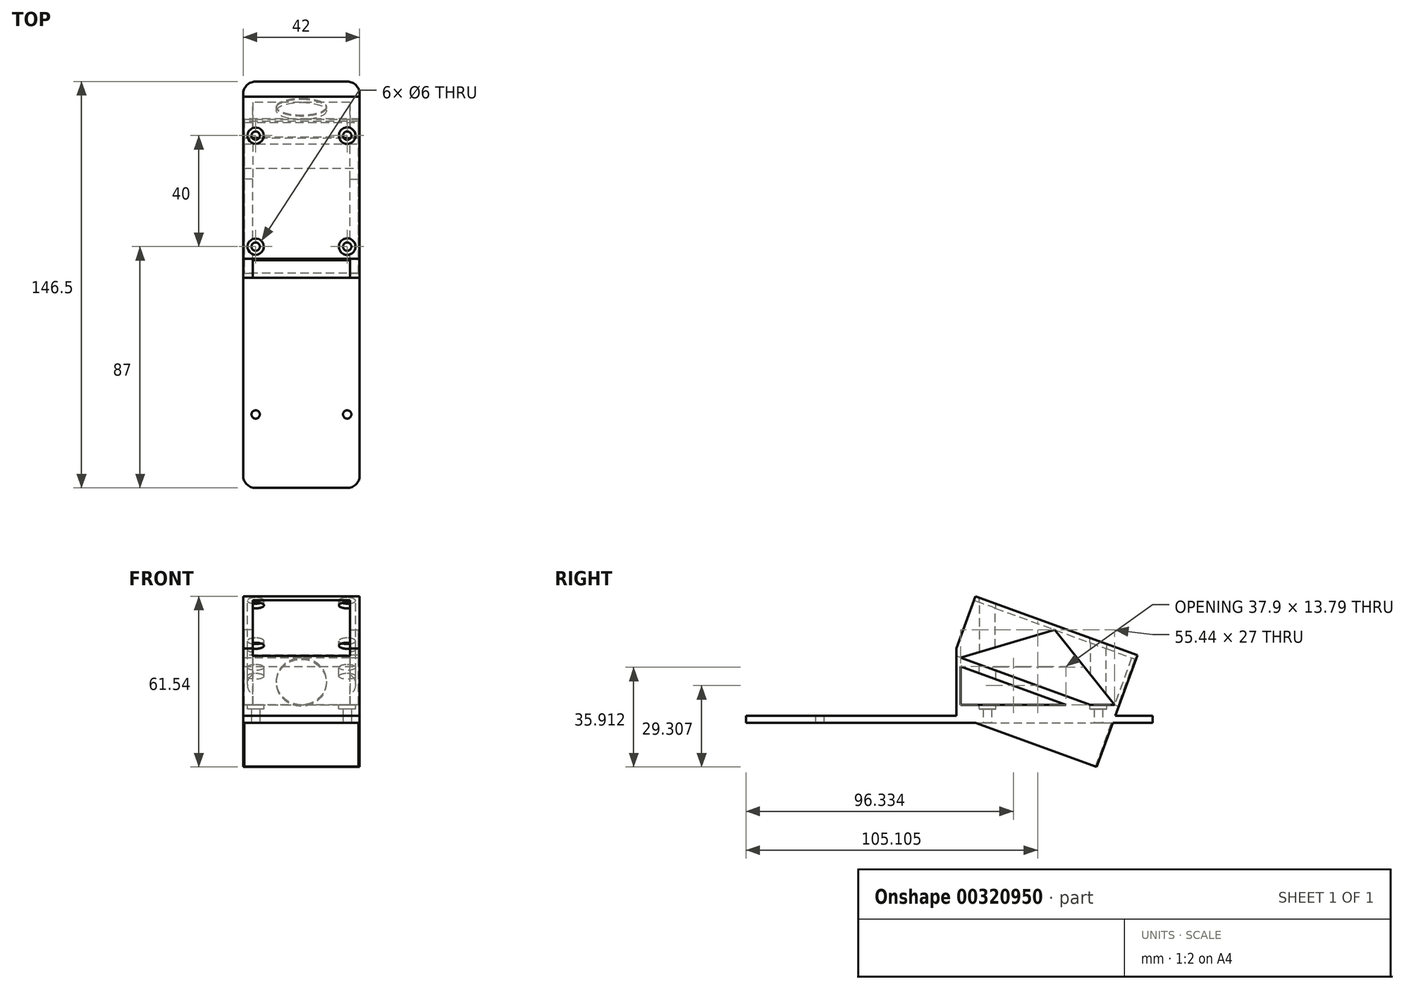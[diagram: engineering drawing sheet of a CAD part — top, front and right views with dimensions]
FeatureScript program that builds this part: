
annotation { "Feature Type Name" : "Feature", "Feature Type Description" : "" }
export const myFeature = defineFeature(function(context is Context, id is Id, definition is map)
    precondition{}
    {
        {
            var Q0;
            Q0=qCreatedBy(makeId("Top.planeOp"),FACE);
            var sketch = newSketch(context, id + "F0", { "sketchPlane" : qUnion([Q0])});
            skLineSegment(sketch, "E0.left", {"start": v(-21, 71.75) * mm, "end": v(-21, -44.25) * mm});
            skLineSegment(sketch, "E0.right", {"start": v(21, 72.25) * mm, "end": v(21, -44.25) * mm});
            skCircle(sketch, "E1", {"center": v(16.5, 72.25) * mm, "radius": 1.5 * mm});
            skCircle(sketch, "E2", {"center": v(-16.5, 72.25) * mm, "radius": 1.5 * mm});
            skCircle(sketch, "E3", {"center": v(16.5, 32.25) * mm, "radius": 1.5 * mm});
            skCircle(sketch, "E4", {"center": v(-16.5, 32.25) * mm, "radius": 1.5 * mm});
            skCircle(sketch, "E5", {"center": v(16.5, -28.25) * mm, "radius": 1.5 * mm});
            skCircle(sketch, "E6", {"center": v(-16.5, -28.25) * mm, "radius": 1.5 * mm});
            skPoint(sketch, "E7", {"position": v(-21, -54.75) * mm});
            skLineSegment(sketch, "E8", {"start": v(-21, -44.25) * mm, "end": v(-21, -50.25) * mm});
            skLineSegment(sketch, "E9", {"start": v(21, -44.25) * mm, "end": v(21, -50.25) * mm});
            skLineSegment(sketch, "E10", {"start": v(16.5, -54.75) * mm, "end": v(-16.5, -54.75) * mm});
            skArc(sketch, "E11.filletArc", {"start": v(-21, -50.25) * mm, "mid": v(-19.68, -53.43) * mm, "end": v(-16.5, -54.75) * mm});
            skPoint(sketch, "E12.visualSharp", {"position": v(21, -54.75) * mm});
            skArc(sketch, "E12.filletArc", {"start": v(16.5, -54.75) * mm, "mid": v(19.68, -53.43) * mm, "end": v(21, -50.25) * mm});
            skLineSegment(sketch, "E13", {"start": v(-21, 71.75) * mm, "end": v(-21, 87.25) * mm});
            skLineSegment(sketch, "E14", {"start": v(-16.5, 91.75) * mm, "end": v(16.5, 91.75) * mm});
            skLineSegment(sketch, "E15", {"start": v(21, 87.25) * mm, "end": v(21, 72.25) * mm});
            skPoint(sketch, "E16.visualSharp", {"position": v(-21, 91.75) * mm});
            skArc(sketch, "E16.filletArc", {"start": v(-16.5, 91.75) * mm, "mid": v(-19.68, 90.43) * mm, "end": v(-21, 87.25) * mm});
            skPoint(sketch, "E17.visualSharp", {"position": v(21, 91.75) * mm});
            skArc(sketch, "E17.filletArc", {"start": v(21, 87.25) * mm, "mid": v(19.68, 90.43) * mm, "end": v(16.5, 91.75) * mm});
            skSolve(sketch);
        }
        {
            var Q0;
            Q0=qSketchRegion(id+"F0",true);
            extrude(context, id + "F1", {"entities" : qUnion([Q0]), "depth" : 2.5 * mm});
        }
        {
            var Q0;
            Q0=qCreatedBy(makeId("Right.planeOp"),FACE);
            var sketch = newSketch(context, id + "F2", { "sketchPlane" : qUnion([Q0])});
            skLineSegment(sketch, "E18.1.1", {"start": v(91.75, 20.68) * mm, "end": v(85.6, 3.76) * mm, "construction": true});
            skLineSegment(sketch, "E18.1.2", {"start": v(22.63, 26.68) * mm, "end": v(28.8, 43.6) * mm});
            skLineSegment(sketch, "E19", {"start": v(84.23, 23.41) * mm, "end": v(78.08, 6.5) * mm});
            skLineSegment(sketch, "E20", {"start": v(28.8, 43.6) * mm, "end": v(84.23, 23.41) * mm});
            skLineSegment(sketch, "E21", {"start": v(91.75, 20.68) * mm, "end": v(85.74, 22.87) * mm, "construction": true});
            skLineSegment(sketch, "E22", {"start": v(85.6, 3.76) * mm, "end": v(79.58, 5.95) * mm, "construction": true});
            skLineSegment(sketch, "E23", {"start": v(22.63, 6.5) * mm, "end": v(22.63, 26.68) * mm});
            skLineSegment(sketch, "E24", {"start": v(79.58, 5.95) * mm, "end": v(78.32, 2.5) * mm});
            skLineSegment(sketch, "E25", {"start": v(78.32, 2.5) * mm, "end": v(22.63, 2.5) * mm});
            skLineSegment(sketch, "E26", {"start": v(86.28, 24.37) * mm, "end": v(26.52, 46.12) * mm});
            skLineSegment(sketch, "E27", {"start": v(79.58, 5.95) * mm, "end": v(86.28, 24.37) * mm});
            skLineSegment(sketch, "E28", {"start": v(27.87, 45.63) * mm, "end": v(21.03, 26.84) * mm});
            skLineSegment(sketch, "E29", {"start": v(22.63, 2.5) * mm, "end": v(21.03, 2.5) * mm});
            skLineSegment(sketch, "E30", {"start": v(21.03, 2.5) * mm, "end": v(21.03, 26.84) * mm});
            skLineSegment(sketch, "E31", {"start": v(78.08, 6.5) * mm, "end": v(22.63, 6.5) * mm});
            skSolve(sketch);
        }
        {
            var Q0;
            Q0=qSketchRegion(id+"F2",true);
            extrude(context, id + "F3", {"entities" : qUnion([Q0]), "depth" : 21 * mm, "hasSecondDirection" : true, "secondDirectionOppositeDirection" : true, "secondDirectionDepth" : 21 * mm});
        }
        {
            var Q0;
            Q0=makeQuery(id+"F3.opExtrude","CAP_FACE",FACE,{"disambiguationData":[OSD([sQuery(id+"F2.wireOp",EDGE,"E18.1.2"),sQuery(id+"F2.wireOp",EDGE,"E19"),sQuery(id+"F2.wireOp",EDGE,"E20"),sQuery(id+"F2.wireOp",EDGE,"E23"),sQuery(id+"F2.wireOp",EDGE,"E24"),sQuery(id+"F2.wireOp",EDGE,"E25"),sQuery(id+"F2.wireOp",EDGE,"E26"),sQuery(id+"F2.wireOp",EDGE,"E27"),sQuery(id+"F2.wireOp",EDGE,"E28"),sQuery(id+"F2.wireOp",EDGE,"E29"),sQuery(id+"F2.wireOp",EDGE,"E30"),sQuery(id+"F2.wireOp",EDGE,"E31")])],"isStart":false});
            var sketch = newSketch(context, id + "F4", { "sketchPlane" : qUnion([Q0])});
            skLineSegment(sketch, "E32", {"start": v(78.08, 6.5) * mm, "end": v(22.63, 26.68) * mm, "construction": true});
            skLineSegment(sketch, "E33", {"start": v(69.3, 6.5) * mm, "end": v(22.63, 23.49) * mm});
            skLineSegment(sketch, "E34", {"start": v(60.53, 6.5) * mm, "end": v(22.63, 20.3) * mm});
            skLineSegment(sketch, "E35", {"start": v(69.3, 6.5) * mm, "end": v(60.53, 6.5) * mm});
            skLineSegment(sketch, "E36", {"start": v(22.63, 20.3) * mm, "end": v(22.63, 23.49) * mm});
            skPoint(sketch, "E37", {"position": v(56.51, 33.5) * mm});
            skLineSegment(sketch, "E38", {"start": v(84.23, 23.41) * mm, "end": v(78.08, 6.5) * mm});
            skLineSegment(sketch, "E39", {"start": v(84.23, 23.41) * mm, "end": v(56.51, 33.5) * mm});
            skLineSegment(sketch, "E40", {"start": v(28.8, 43.6) * mm, "end": v(22.63, 26.68) * mm});
            skLineSegment(sketch, "E41", {"start": v(56.51, 33.5) * mm, "end": v(28.8, 43.6) * mm});
            skLineSegment(sketch, "E42", {"start": v(22.63, 23.49) * mm, "end": v(56.51, 33.5) * mm});
            skLineSegment(sketch, "E43", {"start": v(22.63, 26.68) * mm, "end": v(22.63, 23.49) * mm});
            skLineSegment(sketch, "E44", {"start": v(78.08, 6.5) * mm, "end": v(56.51, 33.5) * mm});
            skSolve(sketch);
        }
        {
            var Q0;
            Q0=makeQuery(id+"F4.imprint","IMPRINT",FACE,{"disambiguationData":[TD([[makeQuery(id+"F4.imprint","IMPRINT",EDGE,{"derivedFrom":sQuery(id+"F4.wireOp",EDGE,"E33")}),1.0]])]});
            extrude(context, id + "F5", {"entities" : qUnion([Q0]), "operationType" : NewBodyOperationType.ADD, "oppositeDirection" : true, "depth" : 42 * mm});
        }
        {
            var Q0;
            Q0=makeQuery(id+"F4.imprint","IMPRINT",FACE,{"disambiguationData":[TD([[makeQuery(id+"F4.imprint","IMPRINT",EDGE,{"derivedFrom":sQuery(id+"F4.wireOp",EDGE,"E38")}),-1.0]])]});
            var Q1;
            Q1=makeQuery(id+"F4.imprint","IMPRINT",FACE,{"disambiguationData":[TD([[makeQuery(id+"F4.imprint","IMPRINT",EDGE,{"derivedFrom":sQuery(id+"F4.wireOp",EDGE,"E40")}),-1.0]])]});
            extrude(context, id + "F6", {"entities" : qUnion([Q0, Q1]), "operationType" : NewBodyOperationType.ADD, "oppositeDirection" : true, "depth" : 3.5 * mm});
        }
        {
            var Q0;
            Q0=makeQuery(id+"F5.boolean.opBoolean","MERGE",FACE,{"derivedFrom":[makeQuery(id+"F3.opExtrude","CAP_FACE",FACE,{"disambiguationData":[OSD([sQuery(id+"F2.wireOp",EDGE,"E18.1.2"),sQuery(id+"F2.wireOp",EDGE,"E19"),sQuery(id+"F2.wireOp",EDGE,"E20"),sQuery(id+"F2.wireOp",EDGE,"E23"),sQuery(id+"F2.wireOp",EDGE,"E24"),sQuery(id+"F2.wireOp",EDGE,"E25"),sQuery(id+"F2.wireOp",EDGE,"E26"),sQuery(id+"F2.wireOp",EDGE,"E27"),sQuery(id+"F2.wireOp",EDGE,"E28"),sQuery(id+"F2.wireOp",EDGE,"E29"),sQuery(id+"F2.wireOp",EDGE,"E30"),sQuery(id+"F2.wireOp",EDGE,"E31")])],"isStart":true}),makeQuery(id+"F5.opExtrude","CAP_FACE",FACE,{"disambiguationData":[OSD([sQuery(id+"F4.wireOp",EDGE,"E33"),sQuery(id+"F4.wireOp",EDGE,"E34"),sQuery(id+"F4.wireOp",EDGE,"E35"),sQuery(id+"F4.wireOp",EDGE,"E36")])],"isStart":false})]});
            var sketch = newSketch(context, id + "F7", { "sketchPlane" : qUnion([Q0])});
            skLineSegment(sketch, "E45.0", {"start": v(-22.63, 23.49) * mm, "end": v(-56.51, 33.5) * mm});
            skLineSegment(sketch, "E45.1", {"start": v(-22.63, 26.68) * mm, "end": v(-28.8, 43.6) * mm});
            skLineSegment(sketch, "E45.2", {"start": v(-22.63, 23.49) * mm, "end": v(-22.63, 26.68) * mm});
            skLineSegment(sketch, "E45.3", {"start": v(-28.8, 43.6) * mm, "end": v(-84.23, 23.41) * mm});
            skLineSegment(sketch, "E45.4", {"start": v(-84.23, 23.41) * mm, "end": v(-78.08, 6.5) * mm});
            skLineSegment(sketch, "E46", {"start": v(-78.08, 6.5) * mm, "end": v(-56.51, 33.5) * mm});
            skLineSegment(sketch, "E47.0", {"start": v(-60.53, 6.5) * mm, "end": v(-22.63, 6.5) * mm, "construction": true});
            skLineSegment(sketch, "E47.1", {"start": v(-87.25, 2.5) * mm, "end": v(50.25, 2.5) * mm, "construction": true});
            skSolve(sketch);
        }
        {
            var Q0;
            {var subQ0=sQuery(id+"F7.wireOp",EDGE,"E45.4");Q0=makeQuery(id+"F7.imprint","IMPRINT",FACE,{"disambiguationData":[TD([[makeQuery(id+"F7.imprint","IMPRINT",EDGE,{"derivedFrom":subQ0}),1.0]])]});}
            var Q1;
            {var subQ0=sQuery(id+"F7.wireOp",EDGE,"E45.0");Q1=makeQuery(id+"F7.imprint","IMPRINT",FACE,{"disambiguationData":[TD([[makeQuery(id+"F7.imprint","IMPRINT",EDGE,{"derivedFrom":subQ0}),-1.0]])]});}
            extrude(context, id + "F8", {"entities" : qUnion([Q0, Q1]), "operationType" : NewBodyOperationType.ADD, "oppositeDirection" : true, "depth" : 3.5 * mm});
        }
        {
            var Q0;
            Q0=makeQuery(id+"F3.opExtrude","SWEPT_FACE",FACE,{"disambiguationData":[OSD([sQuery(id+"F2.wireOp",EDGE,"E24"),sQuery(id+"F2.wireOp",EDGE,"E27")])]});
            var sketch = newSketch(context, id + "F9", { "sketchPlane" : qUnion([Q0])});
            skLineSegment(sketch, "E48.0", {"start": v(-17.5, 32.81) * mm, "end": v(17.5, 32.81) * mm, "construction": true});
            skLineSegment(sketch, "E49.0", {"start": v(-17.5, 50.81) * mm, "end": v(17.5, 50.81) * mm, "construction": true});
            skLineSegment(sketch, "E50.0", {"start": v(17.5, 50.81) * mm, "end": v(17.5, 32.81) * mm, "construction": true});
            skLineSegment(sketch, "E50.1", {"start": v(-17.5, 50.81) * mm, "end": v(-17.5, 32.81) * mm, "construction": true});
            skCircle(sketch, "E51", {"center": v(0, 41.81) * mm, "radius": 9 * mm});
            skPoint(sketch, "E51.centerSnap0", {"position": v(17.5, 41.81) * mm});
            skPoint(sketch, "E51.centerSnap1", {"position": v(0, 32.81) * mm});
            skSolve(sketch);
        }
        {
            var Q0;
            Q0=makeQuery(id+"F9.imprint","IMPRINT",FACE,{"disambiguationData":[TD([[makeQuery(id+"F9.imprint","IMPRINT",EDGE,{"derivedFrom":sQuery(id+"F9.wireOp",EDGE,"E51")}),1.0]])]});
            extrude(context, id + "F10", {"entities" : qUnion([Q0]), "operationType" : NewBodyOperationType.REMOVE, "oppositeDirection" : true, "depth" : 5 * mm});
        }
        {
            var Q0;
            Q0=makeQuery(id+"F3.opExtrude","SWEPT_FACE",FACE,{"disambiguationData":[OSD([sQuery(id+"F2.wireOp",EDGE,"E28")])]});
            var sketch = newSketch(context, id + "F11", { "sketchPlane" : qUnion([Q0])});
            skLineSegment(sketch, "E52.0", {"start": v(-17.5, 32.81) * mm, "end": v(-17.5, 50.81) * mm});
            skLineSegment(sketch, "E52.1", {"start": v(-17.5, 29.81) * mm, "end": v(17.5, 29.81) * mm});
            skLineSegment(sketch, "E52.2", {"start": v(-17.5, 29.81) * mm, "end": v(-17.5, 32.81) * mm});
            skLineSegment(sketch, "E52.3", {"start": v(17.5, 50.81) * mm, "end": v(-17.5, 50.81) * mm});
            skLineSegment(sketch, "E52.4", {"start": v(17.5, 29.81) * mm, "end": v(17.5, 32.81) * mm});
            skLineSegment(sketch, "E52.5", {"start": v(17.5, 32.81) * mm, "end": v(17.5, 50.81) * mm});
            skSolve(sketch);
        }
        {
            var Q0;
            {var subQ5=sQuery(id+"F11.wireOp",EDGE,"E52.0");Q0=makeQuery(id+"F11.imprint","IMPRINT",FACE,{"disambiguationData":[TD([[makeQuery(id+"F11.imprint","IMPRINT",EDGE,{"derivedFrom":subQ5}),-1.0]])]});}
            var Q1;
            {var subQ0=sQuery(id+"F11.wireOp",EDGE,"E52.1");Q1=makeQuery(id+"F11.imprint","IMPRINT",FACE,{"disambiguationData":[TD([[makeQuery(id+"F11.imprint","IMPRINT",EDGE,{"derivedFrom":subQ0}),1.0]])]});}
            extrude(context, id + "F12", {"entities" : qUnion([Q0, Q1]), "operationType" : NewBodyOperationType.REMOVE, "oppositeDirection" : true, "depth" : 5 * mm});
        }
        {
            var Q0;
            {var subQ4=sQuery(id+"F2.wireOp",EDGE,"E31");var subQ12=sQuery(id+"F2.wireOp",EDGE,"E23");Q0=makeQuery(id+"F5.boolean.opBoolean","SPLIT",FACE,{"disambiguationData":[TD([makeQuery(id+"F3.opExtrude","SWEPT_FACE",FACE,{"disambiguationData":[OSD([subQ12])]})])],"derivedFrom":makeQuery(id+"F3.opExtrude","SWEPT_FACE",FACE,{"disambiguationData":[OSD([subQ4])]})});}
            var sketch = newSketch(context, id + "F13", { "sketchPlane" : qUnion([Q0])});
            skCircle(sketch, "E53.0", {"center": v(-16.5, 32.25) * mm, "radius": 1.5 * mm});
            skCircle(sketch, "E53.1", {"center": v(16.5, 32.25) * mm, "radius": 1.5 * mm});
            skCircle(sketch, "E53.2", {"center": v(16.5, 72.25) * mm, "radius": 1.5 * mm});
            skCircle(sketch, "E53.3", {"center": v(-16.5, 72.25) * mm, "radius": 1.5 * mm});
            skSolve(sketch);
        }
        {
            var Q0;
            Q0=qSketchRegion(id+"F13",true);
            extrude(context, id + "F14", {"entities" : qUnion([Q0]), "operationType" : NewBodyOperationType.REMOVE, "oppositeDirection" : true, "depth" : 5 * mm});
        }
        {
            var Q0;
            {var subQ4=sQuery(id+"F2.wireOp",EDGE,"E31");var subQ12=sQuery(id+"F2.wireOp",EDGE,"E23");Q0=makeQuery(id+"F5.boolean.opBoolean","SPLIT",FACE,{"disambiguationData":[TD([makeQuery(id+"F3.opExtrude","SWEPT_FACE",FACE,{"disambiguationData":[OSD([subQ12])]})])],"derivedFrom":makeQuery(id+"F3.opExtrude","SWEPT_FACE",FACE,{"disambiguationData":[OSD([subQ4])]})});}
            var sketch = newSketch(context, id + "F15", { "sketchPlane" : qUnion([Q0])});
            skCircle(sketch, "E54", {"center": v(-16.5, 32.25) * mm, "radius": 3 * mm});
            skCircle(sketch, "E55", {"center": v(16.5, 32.25) * mm, "radius": 3 * mm});
            skLineSegment(sketch, "E56.1.0", {"start": v(21, 60.53) * mm, "end": v(-21, 60.53) * mm, "construction": true});
            skLineSegment(sketch, "E56.1.1", {"start": v(-21, 60.53) * mm, "end": v(-21, 22.63) * mm, "construction": true});
            skLineSegment(sketch, "E56.1.2", {"start": v(-21, 22.63) * mm, "end": v(21, 22.63) * mm, "construction": true});
            skLineSegment(sketch, "E56.1.3", {"start": v(21, 22.63) * mm, "end": v(21, 60.53) * mm, "construction": true});
            skCircle(sketch, "E57.0", {"center": v(-16.5, 72.25) * mm, "radius": 1.5 * mm, "construction": true});
            skCircle(sketch, "E57.1", {"center": v(16.5, 72.25) * mm, "radius": 1.5 * mm, "construction": true});
            skCircle(sketch, "E58", {"center": v(16.5, 72.25) * mm, "radius": 3 * mm});
            skCircle(sketch, "E59", {"center": v(-16.5, 72.25) * mm, "radius": 3 * mm});
            skSolve(sketch);
        }
        {
            var Q0;
            Q0=qSketchRegion(id+"F15",true);
            extrude(context, id + "F16", {"entities" : qUnion([Q0]), "operationType" : NewBodyOperationType.REMOVE, "oppositeDirection" : true, "depth" : 1.5 * mm, "hasSecondDirection" : true, "secondDirectionOppositeDirection" : false, "secondDirectionDepth" : 40 * mm});
        }
        {
            var Q0;
            Q0=makeQuery(id+"F6.boolean.opBoolean","MERGE",FACE,{"derivedFrom":[makeQuery(id+"F5.boolean.opBoolean","MERGE",FACE,{"derivedFrom":[makeQuery(id+"F3.opExtrude","CAP_FACE",FACE,{"disambiguationData":[OSD([sQuery(id+"F2.wireOp",EDGE,"E18.1.2"),sQuery(id+"F2.wireOp",EDGE,"E19"),sQuery(id+"F2.wireOp",EDGE,"E20"),sQuery(id+"F2.wireOp",EDGE,"E23"),sQuery(id+"F2.wireOp",EDGE,"E24"),sQuery(id+"F2.wireOp",EDGE,"E25"),sQuery(id+"F2.wireOp",EDGE,"E26"),sQuery(id+"F2.wireOp",EDGE,"E27"),sQuery(id+"F2.wireOp",EDGE,"E28"),sQuery(id+"F2.wireOp",EDGE,"E29"),sQuery(id+"F2.wireOp",EDGE,"E30"),sQuery(id+"F2.wireOp",EDGE,"E31")])],"isStart":false}),makeQuery(id+"F5.opExtrude","CAP_FACE",FACE,{"disambiguationData":[OSD([sQuery(id+"F4.wireOp",EDGE,"E33"),sQuery(id+"F4.wireOp",EDGE,"E34"),sQuery(id+"F4.wireOp",EDGE,"E35"),sQuery(id+"F4.wireOp",EDGE,"E36")])],"isStart":true})]}),makeQuery(id+"F6.opExtrude","CAP_FACE",FACE,{"disambiguationData":[OSD([sQuery(id+"F4.wireOp",EDGE,"E38"),sQuery(id+"F4.wireOp",EDGE,"E39"),sQuery(id+"F4.wireOp",EDGE,"E44")])],"isStart":true}),makeQuery(id+"F6.opExtrude","CAP_FACE",FACE,{"disambiguationData":[OSD([sQuery(id+"F4.wireOp",EDGE,"E40"),sQuery(id+"F4.wireOp",EDGE,"E41"),sQuery(id+"F4.wireOp",EDGE,"E42"),sQuery(id+"F4.wireOp",EDGE,"E43")])],"isStart":true})]});
            var sketch = newSketch(context, id + "F17", { "sketchPlane" : qUnion([Q0])});
            skLineSegment(sketch, "E60.0", {"start": v(69.3, 6.5) * mm, "end": v(22.63, 23.49) * mm});
            skLineSegment(sketch, "E60.1", {"start": v(22.63, 23.49) * mm, "end": v(56.51, 33.5) * mm});
            skLineSegment(sketch, "E60.2", {"start": v(78.08, 6.5) * mm, "end": v(56.51, 33.5) * mm});
            skLineSegment(sketch, "E60.3", {"start": v(78.08, 6.5) * mm, "end": v(69.3, 6.5) * mm});
            skLineSegment(sketch, "E60.4", {"start": v(60.53, 6.5) * mm, "end": v(22.63, 20.3) * mm});
            skLineSegment(sketch, "E60.5", {"start": v(60.53, 6.5) * mm, "end": v(22.63, 6.5) * mm});
            skLineSegment(sketch, "E60.6", {"start": v(22.63, 6.5) * mm, "end": v(22.63, 20.3) * mm});
            skSolve(sketch);
        }
        {
            var Q0;
            Q0 = qSketchRegion(id + "F17", true);
            extrude(context, id + "F18", {"entities" : qUnion([Q0]), "oppositeDirection" : true, "depth" : .4 * mm});
        }
        {
            var Q0;
            {var subQ0=sQuery(id+"F7.wireOp",EDGE,"E45.3");Q0=makeQuery(id+"F8.boolean.opBoolean","MERGE",FACE,{"derivedFrom":[makeQuery(id+"F5.boolean.opBoolean","MERGE",FACE,{"derivedFrom":[makeQuery(id+"F3.opExtrude","CAP_FACE",FACE,{"disambiguationData":[OSD([sQuery(id+"F2.wireOp",EDGE,"E18.1.2"),sQuery(id+"F2.wireOp",EDGE,"E19"),sQuery(id+"F2.wireOp",EDGE,"E20"),sQuery(id+"F2.wireOp",EDGE,"E23"),sQuery(id+"F2.wireOp",EDGE,"E24"),sQuery(id+"F2.wireOp",EDGE,"E25"),sQuery(id+"F2.wireOp",EDGE,"E26"),sQuery(id+"F2.wireOp",EDGE,"E27"),sQuery(id+"F2.wireOp",EDGE,"E28"),sQuery(id+"F2.wireOp",EDGE,"E29"),sQuery(id+"F2.wireOp",EDGE,"E30"),sQuery(id+"F2.wireOp",EDGE,"E31")])],"isStart":true}),makeQuery(id+"F5.opExtrude","CAP_FACE",FACE,{"disambiguationData":[OSD([sQuery(id+"F4.wireOp",EDGE,"E33"),sQuery(id+"F4.wireOp",EDGE,"E34"),sQuery(id+"F4.wireOp",EDGE,"E35"),sQuery(id+"F4.wireOp",EDGE,"E36")])],"isStart":false})]}),makeQuery(id+"F8.opExtrude","CAP_FACE",FACE,{"disambiguationData":[OSD([sQuery(id+"F7.wireOp",EDGE,"E45.0"),sQuery(id+"F7.wireOp",EDGE,"E45.1"),sQuery(id+"F7.wireOp",EDGE,"E45.2"),subQ0])],"isStart":true}),makeQuery(id+"F8.opExtrude","CAP_FACE",FACE,{"disambiguationData":[OSD([subQ0,sQuery(id+"F7.wireOp",EDGE,"E45.4"),sQuery(id+"F7.wireOp",EDGE,"E46")])],"isStart":true})]});}
            var sketch = newSketch(context, id + "F19", { "sketchPlane" : qUnion([Q0])});
            skLineSegment(sketch, "E61.0", {"start": v(-22.63, 23.49) * mm, "end": v(-56.51, 33.5) * mm});
            skLineSegment(sketch, "E61.1", {"start": v(-78.08, 6.5) * mm, "end": v(-56.51, 33.5) * mm});
            skLineSegment(sketch, "E61.2", {"start": v(-78.08, 6.5) * mm, "end": v(-69.3, 6.5) * mm});
            skLineSegment(sketch, "E61.3", {"start": v(-69.3, 6.5) * mm, "end": v(-22.63, 23.49) * mm});
            skLineSegment(sketch, "E61.4", {"start": v(-60.53, 6.5) * mm, "end": v(-22.63, 20.3) * mm});
            skLineSegment(sketch, "E61.5", {"start": v(-60.53, 6.5) * mm, "end": v(-22.63, 6.5) * mm});
            skLineSegment(sketch, "E61.6", {"start": v(-22.63, 6.5) * mm, "end": v(-22.63, 20.3) * mm});
            skSolve(sketch);
        }
        {
            var Q0;
            Q0 = qSketchRegion(id + "F19", true);
            extrude(context, id + "F20", {"entities" : qUnion([Q0]), "oppositeDirection" : true, "depth" : .4 * mm});
        }
        {
            var Q0;
            Q0=makeQuery(id+"F3.opExtrude","SWEPT_FACE",FACE,{"disambiguationData":[OSD([sQuery(id+"F2.wireOp",EDGE,"E24"),sQuery(id+"F2.wireOp",EDGE,"E27")])]});
            var sketch = newSketch(context, id + "F21", { "sketchPlane" : qUnion([Q0])});
            skCircle(sketch, "E62.0", {"center": v(0, 41.81) * mm, "radius": 9 * mm});
            skSolve(sketch);
        }
        {
            var Q0;
            Q0 = qSketchRegion(id + "F21", true);
            extrude(context, id + "F22", {"entities" : qUnion([Q0]), "oppositeDirection" : true, "depth" : .4 * mm});
        }
        {
            var Q0;
            Q0=qCreatedBy(makeId("Right.planeOp"),FACE);
            var sketch = newSketch(context, id + "F23", { "sketchPlane" : qUnion([Q0])});
            skLineSegment(sketch, "E63.0", {"start": v(86.28, 24.37) * mm, "end": v(78.32, 2.5) * mm, "construction": true});
            skLineSegment(sketch, "E63.1", {"start": v(21.03, 2.5) * mm, "end": v(21.03, 26.84) * mm, "construction": true});
            skLineSegment(sketch, "E63.2", {"start": v(78.32, 2.5) * mm, "end": v(21.03, 2.5) * mm});
            skLineSegment(sketch, "E64", {"start": v(78.32, 2.5) * mm, "end": v(71.62, -15.91) * mm});
            skLineSegment(sketch, "E65", {"start": v(21.03, 2.5) * mm, "end": v(71.62, -15.91) * mm});
            skLineSegment(sketch, "E66", {"start": v(71.25, -15.78) * mm, "end": v(77.9, 2.5) * mm});
            skSolve(sketch);
        }
        {
            var Q0;
            {var subQ0=sQuery(id+"F23.wireOp",EDGE,"E64");Q0=makeQuery(id+"F23.imprint","IMPRINT",FACE,{"disambiguationData":[TD([[makeQuery(id+"F23.imprint","IMPRINT",EDGE,{"derivedFrom":subQ0}),-1.0]])]});}
            extrude(context, id + "F24", {"entities" : qUnion([Q0]), "depth" : 21 * mm, "hasSecondDirection" : true, "secondDirectionOppositeDirection" : true, "secondDirectionDepth" : 21 * mm});
        }
        {
            var Q0;
            {var subQ3=sQuery(id+"F23.wireOp",EDGE,"E66");Q0=makeQuery(id+"F23.imprint","IMPRINT",FACE,{"disambiguationData":[TD([[makeQuery(id+"F23.imprint","IMPRINT",EDGE,{"derivedFrom":subQ3}),1.0]])]});}
            extrude(context, id + "F25", {"entities" : qUnion([Q0]), "operationType" : NewBodyOperationType.ADD, "depth" : 21 * mm, "hasSecondDirection" : true, "secondDirectionOppositeDirection" : false, "secondDirectionDepth" : 20.6 * mm});
        }
        {
            var Q0;
            {var subQ3=sQuery(id+"F23.wireOp",EDGE,"E66");Q0=makeQuery(id+"F23.imprint","IMPRINT",FACE,{"disambiguationData":[TD([[makeQuery(id+"F23.imprint","IMPRINT",EDGE,{"derivedFrom":subQ3}),1.0]])]});}
            extrude(context, id + "F26", {"entities" : qUnion([Q0]), "operationType" : NewBodyOperationType.ADD, "oppositeDirection" : true, "depth" : 21 * mm, "hasSecondDirection" : true, "secondDirectionOppositeDirection" : true, "secondDirectionDepth" : 20.6 * mm});
        }
    });
